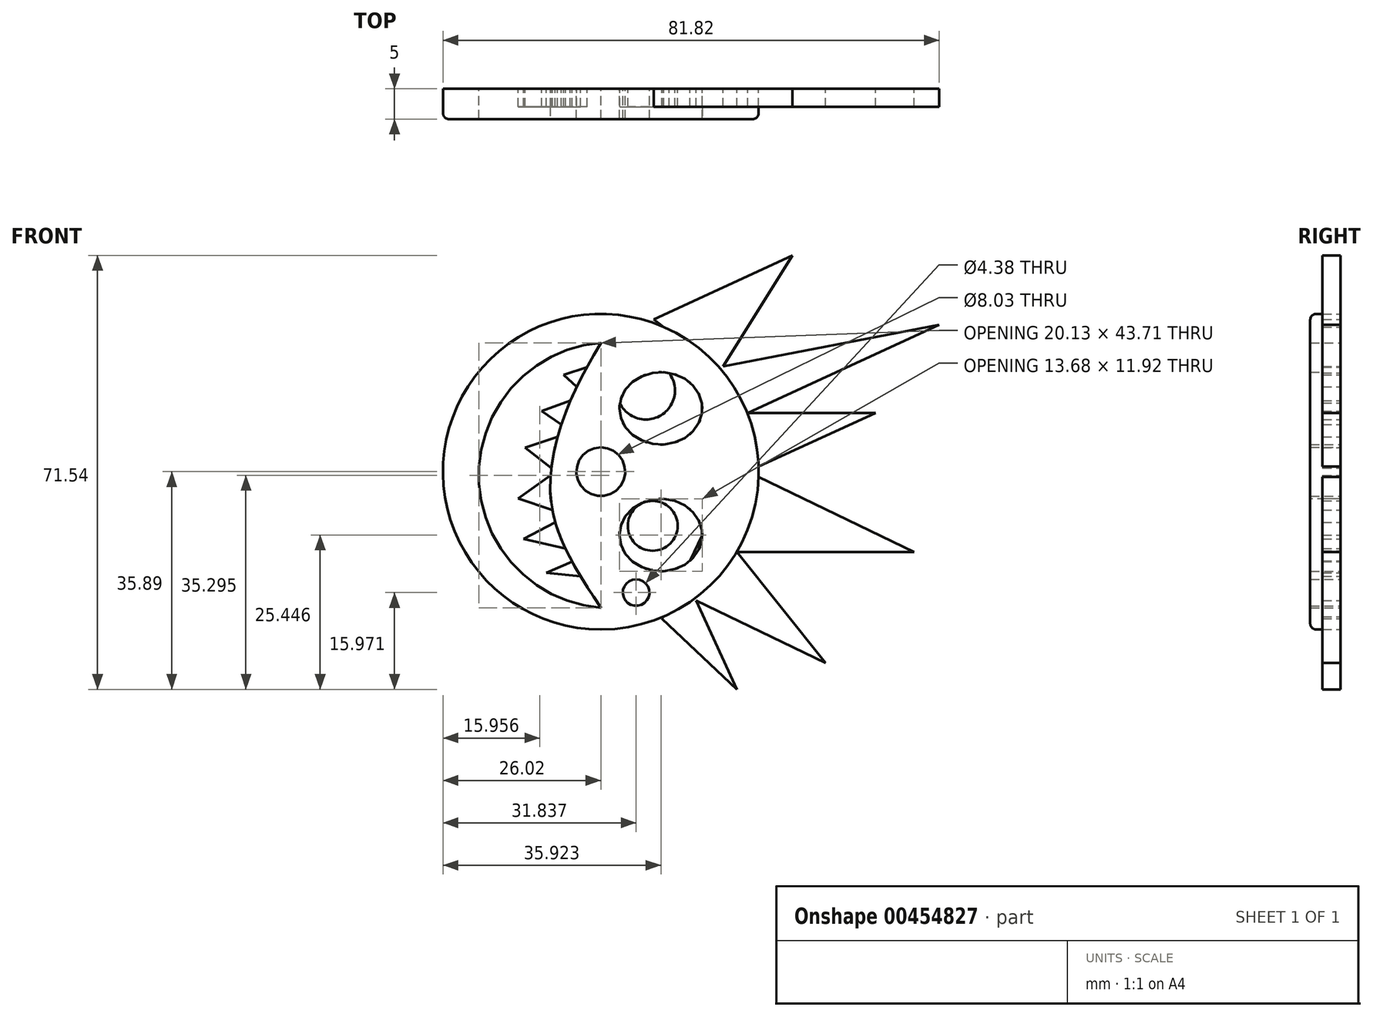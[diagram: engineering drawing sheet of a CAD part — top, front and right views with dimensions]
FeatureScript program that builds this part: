
annotation { "Feature Type Name" : "Feature", "Feature Type Description" : "" }
export const myFeature = defineFeature(function(context is Context, id is Id, definition is map)
    precondition{}
    {
        {
            var Q0;
            Q0=qCreatedBy(makeId("Front.planeOp"),FACE);
            var sketch = newSketch(context, id + "F0", { "sketchPlane" : qUnion([Q0])});
            skCircle(sketch, "E0", {"center": v(0, 0) * mm, "radius": 26.02 * mm});
            skSolve(sketch);
        }
        {
            var Q0;
            Q0 = qSketchRegion(id + "F0", true);
            var Q1;
            Q1 = qSketchRegion(id + "F2", true);
            extrude(context, id + "F1", {"entities" : qUnion([Q0, Q1]), "depth" : 5 * mm});
        }
        {
            var Q0;
            Q0=makeQuery(id+"F1.opExtrude","CAP_FACE",FACE,{"disambiguationData":[OSD([sQuery(id+"F0.wireOp",EDGE,"E0")])],"isStart":true});
            var sketch = newSketch(context, id + "F2", { "sketchPlane" : qUnion([Q0])});
            skEllipse(sketch, "E1", {"center": v(-9.9, 10.44) * mm, "majorRadius": 6.84 * mm, "minorRadius": 5.96 * mm, "majorAxis": v(1, 0)});
            skEllipse(sketch, "E2.MirrorC", {"center": v(-9.9, -10.44) * mm, "majorRadius": 6.84 * mm, "minorRadius": 5.96 * mm, "majorAxis": v(1, 0)});
            skArc(sketch, "E3", {"start": v(0, -22.45) * mm, "mid": v(20.13, -0.6) * mm, "end": v(0, 21.26) * mm});
            skFitSpline(sketch, "E4", {"points": [v(0, 21.26) * mm, v(5.87, 9.64) * mm, v(8.34, -3.34) * mm, v(5.56, -13.22) * mm, v(0, -22.45) * mm], "startDerivative": vector(24.42, -42.5) * mm, "endDerivative": vector(-25.1, -38.11) * mm});
            skCircle(sketch, "E5", {"center": v(0, 0) * mm, "radius": 4.02 * mm});
            skCircle(sketch, "E6", {"center": v(-5.82, -19.92) * mm, "radius": 2.2 * mm});
            skSolve(sketch);
        }
        {
            var Q0;
            Q0 = qSketchRegion(id + "F2", true);
            extrude(context, id + "F3", {"entities" : qUnion([Q0]), "operationType" : NewBodyOperationType.REMOVE, "oppositeDirection" : true, "depth" : 5 * mm});
        }
        {
            var Q0;
            Q0=qCreatedBy(makeId("Front.planeOp"),FACE);
            var sketch = newSketch(context, id + "F4", { "sketchPlane" : qUnion([Q0])});
            skLineSegment(sketch, "E7", {"start": v(8.71, 25.14) * mm, "end": v(31.57, 35.65) * mm});
            skLineSegment(sketch, "E8", {"start": v(31.57, 35.65) * mm, "end": v(20.14, 17.37) * mm});
            skPoint(sketch, "E8.endSnap0", {"position": v(20.14, 30.4) * mm});
            skLineSegment(sketch, "E9", {"start": v(20.14, 17.37) * mm, "end": v(55.8, 24.22) * mm});
            skLineSegment(sketch, "E10", {"start": v(55.8, 24.22) * mm, "end": v(24.24, 9.7) * mm});
            skLineSegment(sketch, "E11", {"start": v(24.24, 9.7) * mm, "end": v(45.29, 9.7) * mm});
            skLineSegment(sketch, "E12", {"start": v(45.29, 9.7) * mm, "end": v(24.19, 0) * mm});
            skLineSegment(sketch, "E13", {"start": v(24.19, 0) * mm, "end": v(51.69, -13.27) * mm});
            skLineSegment(sketch, "E14", {"start": v(51.69, -13.27) * mm, "end": v(22.43, -13.27) * mm});
            skLineSegment(sketch, "E15", {"start": v(22.43, -13.27) * mm, "end": v(37.06, -31.55) * mm});
            skLineSegment(sketch, "E16", {"start": v(37.06, -31.55) * mm, "end": v(15.69, -21.25) * mm});
            skLineSegment(sketch, "E17", {"start": v(15.69, -21.25) * mm, "end": v(22.43, -35.9) * mm});
            skLineSegment(sketch, "E18", {"start": v(22.43, -35.9) * mm, "end": v(10.08, -24.24) * mm});
            skLineSegment(sketch, "E19", {"start": v(10.08, -24.24) * mm, "end": v(20.14, -3.4) * mm});
            skLineSegment(sketch, "E20", {"start": v(20.14, -3.4) * mm, "end": v(17.62, 9.7) * mm});
            skLineSegment(sketch, "E21", {"start": v(17.62, 9.7) * mm, "end": v(15.69, 19.76) * mm});
            skLineSegment(sketch, "E22", {"start": v(15.69, 19.76) * mm, "end": v(8.71, 25.14) * mm});
            skLineSegment(sketch, "E23", {"start": v(0, 18.01) * mm, "end": v(-6.15, 15.98) * mm});
            skLineSegment(sketch, "E24", {"start": v(-6.15, 15.98) * mm, "end": v(-2.45, 12.65) * mm});
            skLineSegment(sketch, "E25", {"start": v(-2.45, 12.65) * mm, "end": v(-9.77, 10) * mm});
            skLineSegment(sketch, "E26", {"start": v(-9.77, 10) * mm, "end": v(-4.76, 6.55) * mm});
            skLineSegment(sketch, "E27", {"start": v(-4.76, 6.55) * mm, "end": v(-12.5, 3.98) * mm});
            skLineSegment(sketch, "E28", {"start": v(-12.5, 3.98) * mm, "end": v(-7.42, 0) * mm});
            skLineSegment(sketch, "E29", {"start": v(-7.42, 0) * mm, "end": v(-13.62, -4.42) * mm});
            skLineSegment(sketch, "E30", {"start": v(-13.62, -4.42) * mm, "end": v(-5.32, -7.18) * mm});
            skLineSegment(sketch, "E31", {"start": v(-5.32, -7.18) * mm, "end": v(-12.75, -11.06) * mm});
            skLineSegment(sketch, "E32", {"start": v(-12.75, -11.06) * mm, "end": v(-4.52, -13) * mm});
            skLineSegment(sketch, "E33", {"start": v(-4.52, -13) * mm, "end": v(-1.91, -13.54) * mm});
            skLineSegment(sketch, "E34", {"start": v(-1.91, -13.54) * mm, "end": v(-9, -16.7) * mm});
            skLineSegment(sketch, "E35", {"start": v(-9, -16.7) * mm, "end": v(0, -17.58) * mm});
            skLineSegment(sketch, "E36", {"start": v(0, 18.01) * mm, "end": v(-2.45, 12.65) * mm});
            skLineSegment(sketch, "E37", {"start": v(-4.76, 6.55) * mm, "end": v(-2.45, 12.65) * mm});
            skLineSegment(sketch, "E38", {"start": v(-4.76, 6.55) * mm, "end": v(-7.42, 0) * mm});
            skLineSegment(sketch, "E39", {"start": v(-5.32, -7.18) * mm, "end": v(-7.42, 0) * mm});
            skLineSegment(sketch, "E40", {"start": v(-5.32, -7.18) * mm, "end": v(-1.91, -13.54) * mm});
            skLineSegment(sketch, "E41", {"start": v(0, -17.58) * mm, "end": v(-1.91, -13.54) * mm});
            skCircle(sketch, "E42", {"center": v(7.44, 13.39) * mm, "radius": 4.78 * mm});
            skCircle(sketch, "E43", {"center": v(8.55, -8.93) * mm, "radius": 4.1 * mm});
            skSolve(sketch);
        }
        {
            var Q0;
            Q0 = qSketchRegion(id + "F4", true);
            extrude(context, id + "F5", {"entities" : qUnion([Q0]), "operationType" : NewBodyOperationType.ADD, "depth" : 3 * mm});
        }
        {
            var Q0;
            Q0=makeQuery(id+"F1.opExtrude","CAP_EDGE",EDGE,{"disambiguationData":[OSD([sQuery(id+"F0.wireOp",EDGE,"E0")])],"isStart":false});
            var Q1;
            Q1=makeQuery(id+"F3.boolean.opBoolean","COPY",EDGE,{"derivedFrom":makeQuery(id+"F3.opExtrude","CAP_EDGE",EDGE,{"disambiguationData":[OSD([sQuery(id+"F2.wireOp",EDGE,"E2.MirrorC")])],"isStart":false})});
            var Q2;
            Q2=makeQuery(id+"F3.boolean.opBoolean","COPY",EDGE,{"derivedFrom":makeQuery(id+"F3.opExtrude","CAP_EDGE",EDGE,{"disambiguationData":[OSD([sQuery(id+"F2.wireOp",EDGE,"E1")])],"isStart":false})});
            var Q3;
            Q3=makeQuery(id+"F3.boolean.opBoolean","COPY",EDGE,{"derivedFrom":makeQuery(id+"F3.opExtrude","CAP_EDGE",EDGE,{"disambiguationData":[OSD([sQuery(id+"F2.wireOp",EDGE,"E3")])],"isStart":false})});
            var Q4;
            Q4=makeQuery(id+"F3.boolean.opBoolean","COPY",EDGE,{"derivedFrom":makeQuery(id+"F3.opExtrude","CAP_EDGE",EDGE,{"disambiguationData":[OSD([sQuery(id+"F2.wireOp",EDGE,"E4")])],"isStart":false})});
            var Q5;
            Q5=makeQuery(id+"F3.boolean.opBoolean","COPY",EDGE,{"derivedFrom":makeQuery(id+"F3.opExtrude","CAP_EDGE",EDGE,{"disambiguationData":[OSD([sQuery(id+"F2.wireOp",EDGE,"E6")])],"isStart":false})});
            var Q6;
            Q6=makeQuery(id+"F3.boolean.opBoolean","COPY",EDGE,{"derivedFrom":makeQuery(id+"F3.opExtrude","CAP_EDGE",EDGE,{"disambiguationData":[OSD([sQuery(id+"F2.wireOp",EDGE,"E5")])],"isStart":false})});
            fillet(context, id + "F6", {"entities" : qUnion([Q0, Q1, Q2, Q3, Q4, Q5, Q6]), "radius" : 1 * mm, "tangentPropagation" : true, "allowEdgeOverflow" : false});
        }
    });
